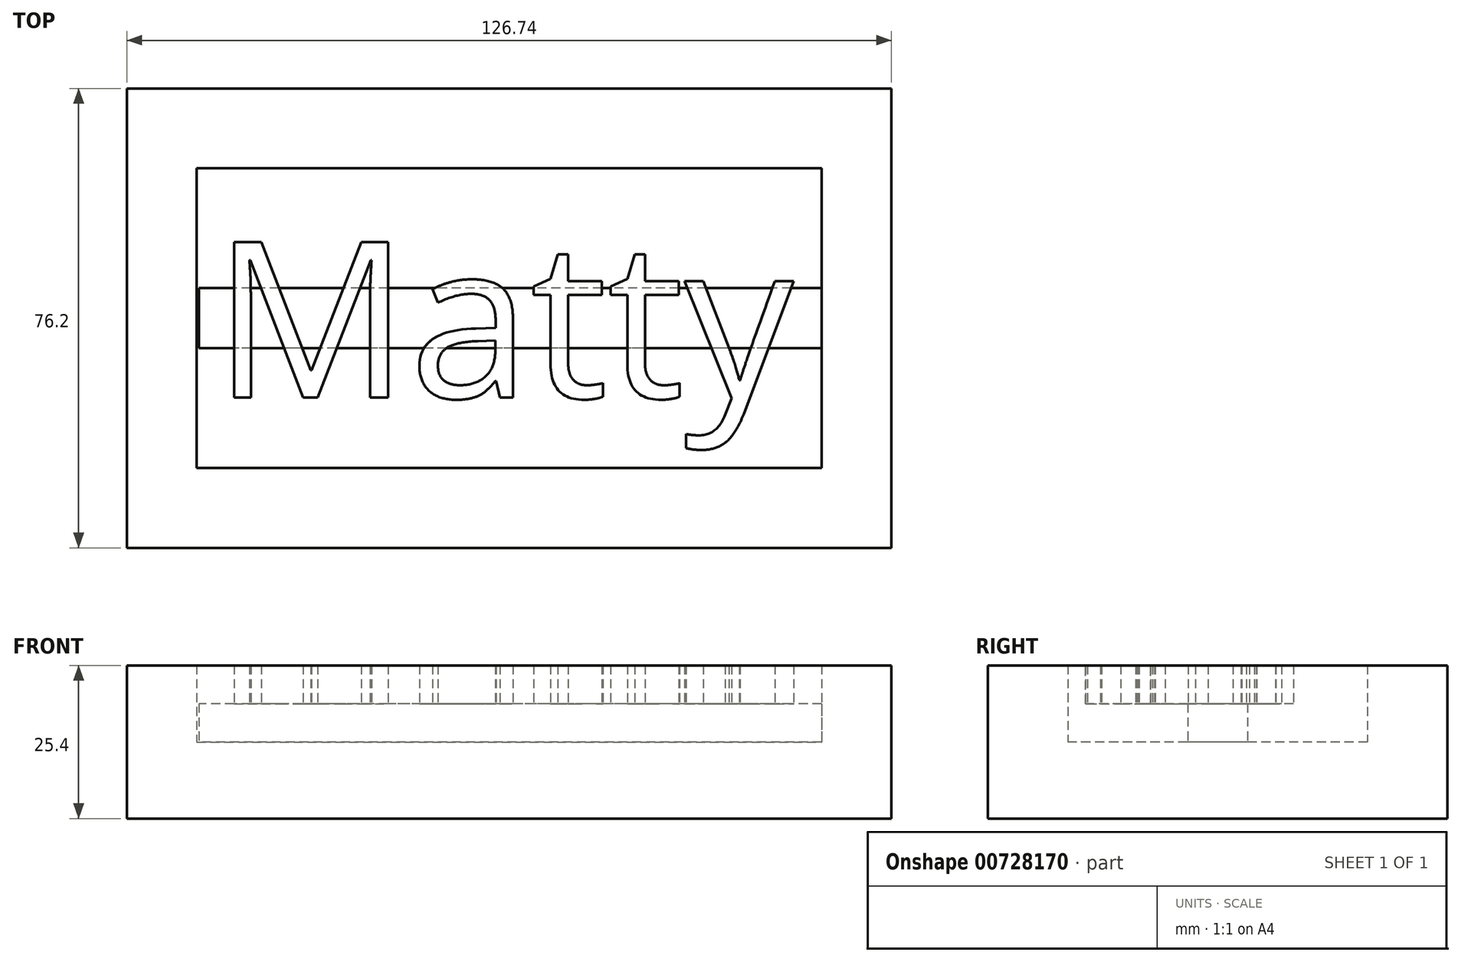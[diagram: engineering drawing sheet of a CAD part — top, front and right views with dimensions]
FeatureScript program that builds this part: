
annotation { "Feature Type Name" : "Feature", "Feature Type Description" : "" }
export const myFeature = defineFeature(function(context is Context, id is Id, definition is map)
    precondition{}
    {
        {
            var Q0;
            Q0=qCreatedBy(makeId("Top.planeOp"),FACE);
            var sketch = newSketch(context, id + "F0", { "sketchPlane" : qUnion([Q0])});
            skLineSegment(sketch, "E0.bottom", {"start": v(-63.37, 38.1) * mm, "end": v(63.37, 38.1) * mm});
            skLineSegment(sketch, "E0.top", {"start": v(-63.37, -38.1) * mm, "end": v(63.37, -38.1) * mm});
            skLineSegment(sketch, "E0.left", {"start": v(-63.37, 38.1) * mm, "end": v(-63.37, -38.1) * mm});
            skLineSegment(sketch, "E0.right", {"start": v(63.37, 38.1) * mm, "end": v(63.37, -38.1) * mm});
            skPoint(sketch, "E0.middle", {"position": v(0, 0) * mm});
            skLineSegment(sketch, "E1.bottom", {"start": v(-51.81, 24.85) * mm, "end": v(51.81, 24.85) * mm});
            skLineSegment(sketch, "E1.top", {"start": v(-51.81, -24.85) * mm, "end": v(51.81, -24.85) * mm});
            skLineSegment(sketch, "E1.left", {"start": v(-51.81, 24.85) * mm, "end": v(-51.81, -24.85) * mm});
            skLineSegment(sketch, "E1.right", {"start": v(51.81, 24.85) * mm, "end": v(51.81, -24.85) * mm});
            skSolve(sketch);
        }
        {
            var Q0;
            Q0=makeQuery(id+"F0.imprint","IMPRINT",FACE,{"disambiguationData":[TD([[makeQuery(id+"F0.imprint","IMPRINT",EDGE,{"derivedFrom":sQuery(id+"F0.wireOp",EDGE,"E0.bottom")}),-1.0]])]});
            extrude(context, id + "F1", {"entities" : qUnion([Q0]), "depth" : 25.4 * mm, "offsetDistance" : 25.4 * mm});
        }
        {
            var Q0;
            Q0=makeQuery(id+"F0.imprint","IMPRINT",FACE,{"disambiguationData":[TD([[makeQuery(id+"F0.imprint","IMPRINT",EDGE,{"derivedFrom":sQuery(id+"F0.wireOp",EDGE,"E1.bottom")}),-1.0]])]});
            extrude(context, id + "F2", {"entities" : qUnion([Q0]), "operationType" : NewBodyOperationType.ADD, "depth" : 12.7 * mm, "offsetDistance" : 25.4 * mm});
        }
        {
            var Q0;
            Q0=makeQuery(id+"F2.opExtrude","CAP_FACE",FACE,{"disambiguationData":[OSD([sQuery(id+"F0.wireOp",EDGE,"E1.bottom"),sQuery(id+"F0.wireOp",EDGE,"E1.top"),sQuery(id+"F0.wireOp",EDGE,"E1.left"),sQuery(id+"F0.wireOp",EDGE,"E1.right")])],"isStart":false});
            var sketch = newSketch(context, id + "F3", { "sketchPlane" : qUnion([Q0])});
            skLineSegment(sketch, "E2.bottom", {"start": v(51.81, 4.97) * mm, "end": v(-51.43, 4.97) * mm});
            skLineSegment(sketch, "E2.top", {"start": v(51.81, -4.97) * mm, "end": v(-51.43, -4.97) * mm});
            skLineSegment(sketch, "E2.left", {"start": v(51.81, 4.97) * mm, "end": v(51.81, -4.97) * mm});
            skLineSegment(sketch, "E2.right", {"start": v(-51.43, 4.97) * mm, "end": v(-51.43, -4.97) * mm});
            skPoint(sketch, "E2.middle", {"position": v(0.2, 0) * mm});
            skSolve(sketch);
        }
        {
            var Q0;
            Q0=makeQuery(id+"F3.imprint","IMPRINT",FACE,{"disambiguationData":[TD([[makeQuery(id+"F3.imprint","IMPRINT",EDGE,{"derivedFrom":sQuery(id+"F3.wireOp",EDGE,"E2.bottom")}),1.0]])]});
            extrude(context, id + "F4", {"entities" : qUnion([Q0]), "operationType" : NewBodyOperationType.ADD, "depth" : 6.35 * mm, "offsetDistance" : 25.4 * mm});
        }
        {
            var Q0;
            Q0=makeQuery(id+"F4.opExtrude","CAP_FACE",FACE,{"disambiguationData":[OSD([sQuery(id+"F3.wireOp",EDGE,"E2.bottom"),sQuery(id+"F3.wireOp",EDGE,"E2.top"),sQuery(id+"F3.wireOp",EDGE,"E2.left"),sQuery(id+"F3.wireOp",EDGE,"E2.right")])],"isStart":false});
            var sketch = newSketch(context, id + "F5", { "sketchPlane" : qUnion([Q0])});
            skText(sketch, "E3", { "text": "Matty", "fontName": "OpenSans-Regular.ttf"});
            const initialGuessF5  = {"E3": [-0.04914, -0.0132, 1, 0, 0.026]};
            skSetInitialGuess(sketch, initialGuessF5);
            skSolve(sketch);
        }
        {
            var Q0;
            Q0 = qSketchRegion(id + "F5", true);
            extrude(context, id + "F6", {"entities" : qUnion([Q0]), "operationType" : NewBodyOperationType.ADD, "depth" : 6.35 * mm, "offsetDistance" : 25.4 * mm});
        }
    });
